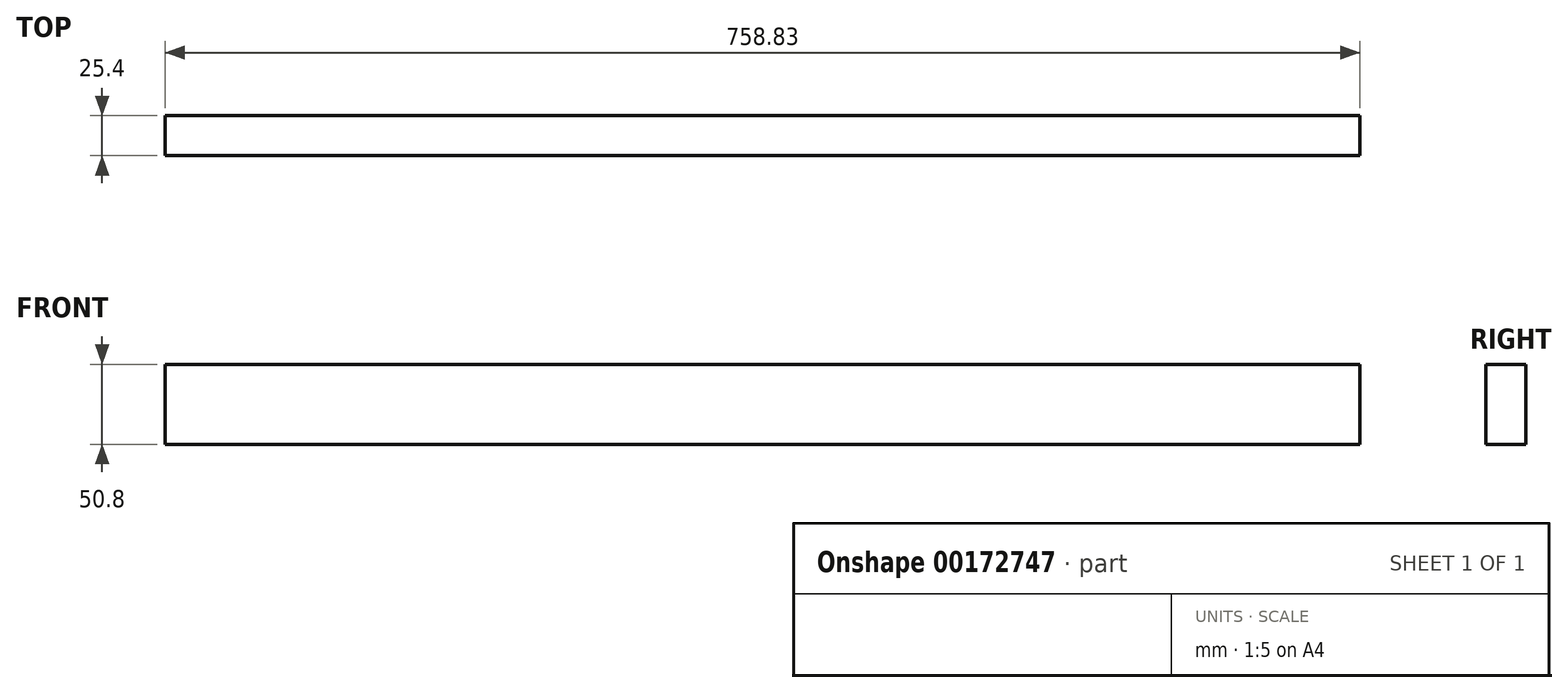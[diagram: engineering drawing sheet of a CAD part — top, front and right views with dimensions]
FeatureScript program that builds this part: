
annotation { "Feature Type Name" : "Feature", "Feature Type Description" : "" }
export const myFeature = defineFeature(function(context is Context, id is Id, definition is map)
    precondition{}
    {
        {
            var Q0;
            Q0=qCreatedBy(makeId("Front.planeOp"),FACE);
            var sketch = newSketch(context, id + "F0", { "sketchPlane" : qUnion([Q0])});
            skLineSegment(sketch, "E0.bottom", {"start": v(-338.59, 50.8) * mm, "end": v(420.24, 50.8) * mm});
            skLineSegment(sketch, "E0.top", {"start": v(-338.59, 0) * mm, "end": v(420.24, 0) * mm});
            skLineSegment(sketch, "E0.left", {"start": v(-338.59, 50.8) * mm, "end": v(-338.59, 0) * mm});
            skLineSegment(sketch, "E0.right", {"start": v(420.24, 50.8) * mm, "end": v(420.24, 0) * mm});
            skSolve(sketch);
        }
        {
            var Q0;
            Q0 = qSketchRegion(id + "F0", true);
            extrude(context, id + "F1", {"entities" : qUnion([Q0]), "depth" : 25.4 * mm});
        }
    });
